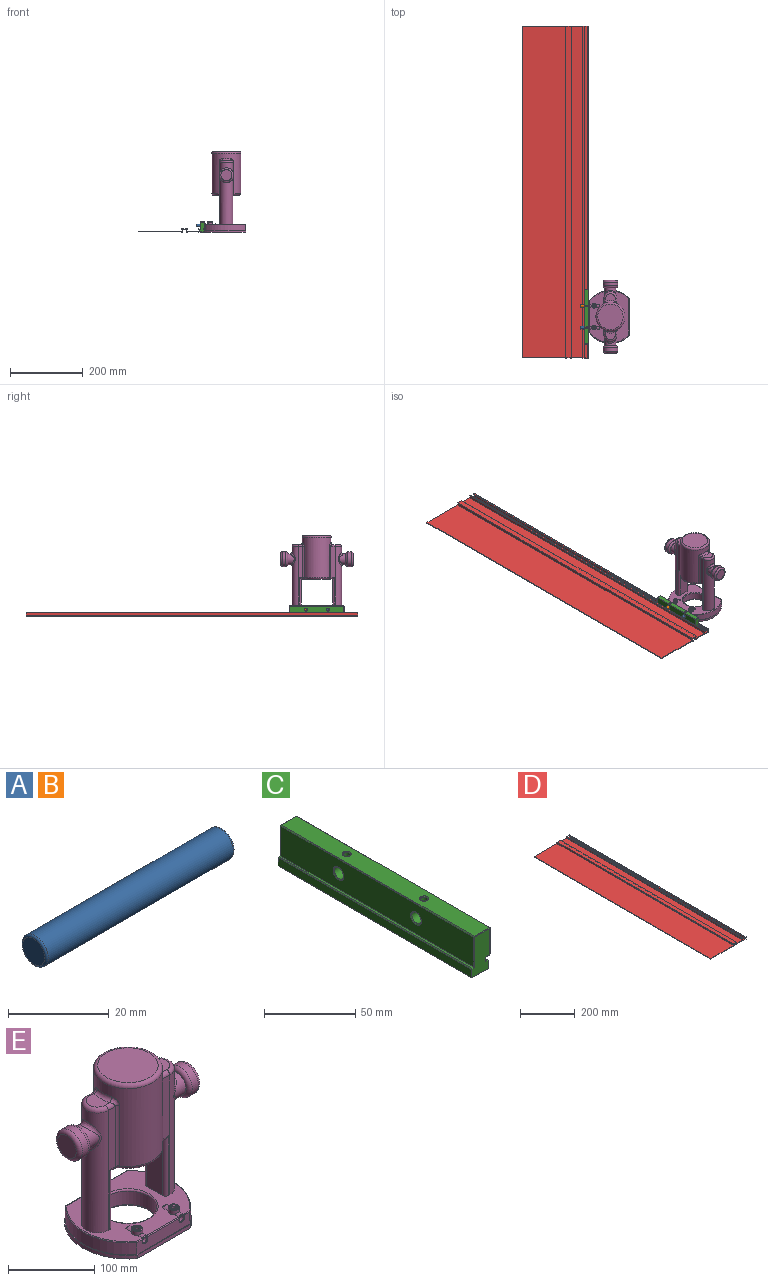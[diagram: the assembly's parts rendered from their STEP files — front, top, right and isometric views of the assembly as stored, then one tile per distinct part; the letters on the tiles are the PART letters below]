
ASSEMBLY  parts=5 mates=7
PART A: 5 faces, bbox 53x7.8x7.8 mm
  f0: cylinder r=3.6mm len=52mm, axis (-1,0,0), area 1174.6mm2, adj f3,f4
  f1: plane 6.19x6.19mm, normal (1,0,0), area 30.1mm2, adj f4
  f2: plane 6.19x6.19mm, normal (-1,0,0), area 30.1mm2, adj f3
  f3: torus R=3.1mm, axis (1,0,0), area 16.8mm2, adj f0,f2
  f4: torus R=3.1mm, axis (1,0,0), area 16.8mm2, adj f0,f1
PART B: same geometry as A
PART C: 48 faces, bbox 14.5x150x27 mm
  f0: plane 149x11.75mm, normal (0,0,1), area 1710.7mm2, adj f25,f28,f29,f30,f42,f43
  f1: cylinder r=3.65mm len=11.75mm, axis (1,0,0), area 256.1mm2, adj f14,f44,f47
  f2: plane 149x17.49mm, normal (1,0,0), area 2497.8mm2, adj f30,f33,f34,f35,f46,f47
  f3: plane 149x20mm, normal (-1,0,0), area 2871.9mm2, adj f4,f23,f24,f25,f44,f45
  f4: plane 149x1.25mm, normal (0,0,1), area 186.3mm2, adj f3,f20,f21,f22
  f5: plane 150x5.5mm, normal (-1,0,0), area 824.7mm2, adj f10,f11,f20,f39
  f6: plane 149x11.5mm, normal (0,0,-1), area 1713.2mm2, adj f38,f39,f40,f41
  f7: plane 150x5.5mm, normal (1,0,0), area 824.7mm2, adj f10,f11,f18,f40
  f8: plane 149x1.25mm, normal (0,0,1), area 186.2mm2, adj f9,f17,f18,f19
  f9: plane 149.5x3.01mm, normal (1,0,0), area 300.9mm2, adj f8,f11,f12,f16,f19,f37
  f10: plane 26x14mm, normal (0,1,0), area 300.2mm2, adj f5,f7,f12,f16,f17,f21,f23,f28
  f11: plane 26x14mm, normal (0,-1,0), area 299.8mm2, adj f5,f7,f9,f19,f22,f24,f29,f34
  f12: plane 149.5x3.75mm, normal (0,0,-1), area 486.1mm2, adj f9,f10,f16,f35,f37
  f13: cylinder r=3.65mm len=11.75mm, axis (1,0,0), area 256.1mm2, adj f15,f45,f46
  f14: cylinder r=2.02mm len=6.46mm, axis (0,0,1), area 78mm2, adj f1,f43
  f15: cylinder r=2.02mm len=6.46mm, axis (0,0,1), area 78mm2, adj f13,f42
  f16: plane 2.51x0.5mm, normal (0.71,0.71,0), area 1.6mm2, adj f9,f10,f12,f17
  f17: plane 2.25x0.5mm, normal (0,0.71,0.71), area 1.2mm2, adj f8,f10,f16,f18
  f18: plane 150x0.5mm, normal (0.71,0,0.71), area 105.7mm2, adj f7,f8,f17,f19
  f19: plane 1.75x0.5mm, normal (0,-0.71,0.71), area 1.1mm2, adj f8,f9,f11,f18
  f20: plane 150x0.5mm, normal (-0.71,0,0.71), area 105.7mm2, adj f4,f5,f21,f22
  f21: plane 2.25x0.5mm, normal (0,0.71,0.71), area 1.2mm2, adj f4,f10,f20,f23
  f22: plane 2.25x0.5mm, normal (0,-0.71,0.71), area 1.2mm2, adj f4,f11,f20,f24
  f23: plane 20.5x0.5mm, normal (-0.71,0.71,0), area 14.3mm2, adj f3,f10,f21,f26
  f24: plane 20.5x0.5mm, normal (-0.71,-0.71,0), area 14.3mm2, adj f3,f11,f22,f27
  f25: plane 149x0.5mm, normal (-0.71,0,0.71), area 105.4mm2, adj f0,f3,f26,f27
  f26: plane 0.5x0.5mm, normal (-0.58,0.58,0.58), area 0.2mm2, adj f23,f25,f28
  f27: plane 0.5x0.5mm, normal (-0.58,-0.58,0.58), area 0.2mm2, adj f24,f25,f29
  f28: plane 11.75x0.5mm, normal (0,0.71,0.71), area 8.3mm2, adj f0,f10,f26,f31
  f29: plane 11.75x0.5mm, normal (0,-0.71,0.71), area 8.3mm2, adj f0,f11,f27,f32
  f30: plane 149x0.5mm, normal (0.71,0,0.71), area 105.4mm2, adj f0,f2,f31,f32
  f31: plane 0.5x0.5mm, normal (0.58,0.58,0.58), area 0.2mm2, adj f28,f30,f33
  f32: plane 0.5x0.5mm, normal (0.58,-0.58,0.58), area 0.2mm2, adj f29,f30,f34
  f33: plane 17.99x0.5mm, normal (0.71,0.71,0), area 12.5mm2, adj f2,f10,f31,f35
  f34: plane 17.49x0.5mm, normal (0.71,-0.71,0), area 12.4mm2, adj f2,f11,f32,f36
  f35: plane 149.5x0.5mm, normal (0.71,0,-0.71), area 105.5mm2, adj f2,f12,f33,f36
  f36: plane 0.5x0.5mm, normal (0.58,-0.58,-0.58), area 0.2mm2, adj f34,f35,f37
  f37: plane 3.25x0.5mm, normal (0,-0.71,-0.71), area 2.3mm2, adj f9,f11,f12,f36
  f38: plane 12.5x0.5mm, normal (0,-0.71,-0.71), area 8.5mm2, adj f6,f11,f39,f40
  f39: plane 150x0.5mm, normal (-0.71,0,-0.71), area 105.7mm2, adj f5,f6,f38,f41
  f40: plane 150x0.5mm, normal (0.71,0,-0.71), area 105.7mm2, adj f6,f7,f38,f41
  f41: plane 12.5x0.5mm, normal (0,0.71,-0.71), area 8.5mm2, adj f6,f10,f39,f40
  f42: torus R=2.52mm, axis (0,0,-1), area 10.9mm2, adj f0,f15
  f43: torus R=2.52mm, axis (0,0,-1), area 10.9mm2, adj f0,f14
  f44: torus R=4.15mm, axis (1,0,0), area 18.9mm2, adj f1,f3
  f45: torus R=4.15mm, axis (1,0,0), area 18.9mm2, adj f3,f13
  f46: torus R=4.15mm, axis (1,0,0), area 18.9mm2, adj f2,f13
  f47: torus R=4.15mm, axis (1,0,0), area 18.9mm2, adj f1,f2
PART D: 34 faces, bbox 183.5x914.4x10.5 mm
  f0: plane 914.4x3.75mm, normal (0,0,1), area 3429mm2, adj f1,f31,f32,f33
  f1: plane 914.4x6.5mm, normal (-1,0,0), area 5943.6mm2, adj f0,f2,f32,f33
  f2: plane 914.4x32mm, normal (0,0,1), area 29260.8mm2, adj f1,f3,f32,f33
  f3: plane 914.4x6.5mm, normal (1,0,0), area 5943.6mm2, adj f2,f4,f32,f33
  f4: plane 914.4x16mm, normal (0,0,1), area 14630.4mm2, adj f3,f5,f32,f33
  f5: plane 914.4x6.5mm, normal (-1,0,0), area 5943.6mm2, adj f4,f6,f32,f33
  f6: plane 914.4x119mm, normal (0,0,1), area 108813.6mm2, adj f5,f7,f32,f33
  f7: plane 914.4x2mm, normal (-1,0,0), area 1828.8mm2, adj f6,f8,f32,f33
  f8: plane 914.4x119mm, normal (0,0,-1), area 108813.6mm2, adj f7,f9,f32,f33
  f9: plane 914.4x2mm, normal (-1,0,0), area 1828.8mm2, adj f8,f10,f32,f33
  f10: plane 914.4x3.75mm, normal (0,0,-1), area 3429mm2, adj f9,f11,f32,f33
  f11: plane 914.4x2mm, normal (1,0,0), area 1828.8mm2, adj f10,f12,f32,f33
  f12: plane 914.4x1.75mm, normal (0,0,1), area 1600.2mm2, adj f11,f13,f32,f33
  f13: plane 914.4x6.5mm, normal (1,0,0), area 5943.6mm2, adj f12,f14,f32,f33
  f14: plane 914.4x12mm, normal (0,0,-1), area 10972.8mm2, adj f13,f15,f32,f33
  f15: plane 914.4x6.5mm, normal (-1,0,0), area 5943.6mm2, adj f14,f16,f32,f33
  f16: plane 914.4x1.75mm, normal (0,0,1), area 1600.2mm2, adj f15,f17,f32,f33
  f17: plane 914.4x2mm, normal (-1,0,0), area 1828.8mm2, adj f16,f18,f32,f33
  f18: plane 914.4x3.75mm, normal (0,0,-1), area 3429mm2, adj f17,f19,f32,f33
  f19: plane 914.4x2mm, normal (1,0,0), area 1828.8mm2, adj f18,f20,f32,f33
  f20: plane 914.4x32mm, normal (0,0,-1), area 29260.8mm2, adj f19,f21,f32,f33
  f21: plane 914.4x2mm, normal (-1,0,0), area 1828.8mm2, adj f20,f22,f32,f33
  f22: plane 914.4x16.5mm, normal (0,0,-1), area 15087.6mm2, adj f21,f23,f32,f33
  f23: plane 914.4x10.5mm, normal (1,0,0), area 9601.2mm2, adj f22,f24,f32,f33
  f24: plane 914.4x3.75mm, normal (0,0,1), area 3429mm2, adj f23,f25,f32,f33
  f25: plane 914.4x2mm, normal (-1,0,0), area 1828.8mm2, adj f24,f26,f32,f33
  f26: plane 914.4x1.75mm, normal (0,0,-1), area 1600.2mm2, adj f25,f27,f32,f33
  f27: plane 914.4x6.5mm, normal (-1,0,0), area 5943.6mm2, adj f26,f28,f32,f33
  f28: plane 914.4x12.5mm, normal (0,0,1), area 11430mm2, adj f27,f29,f32,f33
  f29: plane 914.4x6.5mm, normal (1,0,0), area 5943.6mm2, adj f28,f30,f32,f33
  f30: plane 914.4x1.75mm, normal (0,0,-1), area 1600.2mm2, adj f29,f31,f32,f33
  f31: plane 914.4x2mm, normal (1,0,0), area 1828.8mm2, adj f0,f30,f32,f33
  f32: plane 183.5x10.5mm, normal (0,-1,0), area 449mm2, adj f0,f1,f2,f3,f4,f5,f6,f7
  f33: plane 183.5x10.5mm, normal (0,1,0), area 449mm2, adj f0,f1,f2,f3,f4,f5,f6,f7
PART E: 108 faces, bbox 200.6x119.7x223.6 mm
  f0: cylinder r=3.6mm len=28mm, axis (0,-1,0), area 607.3mm2, adj f89,f90,f97
  f1: plane 86.74x17mm, normal (0,-1,0), area 1357.1mm2, adj f15,f21,f23,f95,f97,f100,f102,f103
  f2: plane 143.61x108.61mm, normal (0,0,1), area 7962.3mm2, adj f3,f4,f5,f7,f8,f9,f10,f27
  f3: cylinder r=6.25mm len=12.5mm, axis (0,0,-1), area 209.6mm2, adj f2,f84,f86,f106
  f4: cylinder r=18mm len=170mm, axis (0,0,-1), area 8490.4mm2, adj f2,f7,f8,f42,f69
  f5: cylinder r=18mm len=170mm, axis (0,0,-1), area 8490.4mm2, adj f2,f9,f10,f33,f75
  f6: cylinder r=40mm len=110.52mm, axis (0,0,-1), area 19663.1mm2, adj f32,f34,f36,f37,f38,f39,f41,f43
  f7: plane 170x11.66mm, normal (0,-1,0), area 1163.2mm2, adj f2,f4,f44,f46,f47,f56
  f8: plane 170x11.66mm, normal (0,1,0), area 1163.2mm2, adj f2,f4,f39,f40,f48,f57
  f9: plane 170x11.66mm, normal (0,1,0), area 1163.2mm2, adj f2,f5,f31,f32,f49,f61
  f10: plane 170x11.66mm, normal (0,-1,0), area 1163.2mm2, adj f2,f5,f35,f38,f50,f52
  f11: plane 87.07x5mm, normal (0,-1,0), area 435.4mm2, adj f15,f16,f17,f20
  f12: cylinder r=73.5mm len=111.76mm, axis (0,0,-1), area 636.7mm2, adj f15,f16,f17,f18
  f13: plane 101.65x5mm, normal (0,1,0), area 508.2mm2, adj f15,f16,f18,f19
  f14: cylinder r=73.5mm len=111.76mm, axis (0,0,-1), area 636.7mm2, adj f15,f16,f19,f20
  f15: plane 147x112mm, normal (0,0,1), area 441.6mm2, adj f1,f11,f12,f13,f14,f17,f18,f19
  f16: plane 147x112mm, normal (0,0,-1), area 10820.1mm2, adj f11,f12,f13,f14,f17,f18,f19,f20
  f17: cylinder r=0.5mm len=5mm, axis (0,0,-1), area 1.6mm2, adj f11,f12,f15,f16
  f18: cylinder r=0.5mm len=5mm, axis (0,0,-1), area 1.9mm2, adj f12,f13,f15,f16
  f19: cylinder r=0.5mm len=5mm, axis (0,0,-1), area 1.9mm2, adj f13,f14,f15,f16
  f20: cylinder r=0.5mm len=5mm, axis (0,0,-1), area 1.6mm2, adj f11,f14,f15,f16
  f21: cylinder r=72.5mm len=110mm, axis (0,0,-1), area 2129.1mm2, adj f1,f15,f22,f99
  f22: plane 101.24x17mm, normal (0,1,0), area 1721.1mm2, adj f15,f21,f23,f96
  f23: cylinder r=72.5mm len=110mm, axis (0,0,-1), area 2129.1mm2, adj f1,f15,f22,f94
  f24: plane 70x70mm, normal (0,0,1), area 3848.5mm2, adj f51
  f25: plane 26x20.26mm, normal (0,0,1), area 420.7mm2, adj f40,f42,f43,f44
  f26: plane 26x20.26mm, normal (0,0,1), area 420.7mm2, adj f31,f33,f35,f36
  f27: plane 79.48x26mm, normal (-1,0,0), area 2066.6mm2, adj f2,f28,f47,f48
  f28: plane 86.74x70mm, normal (0,0,-1), area 4350.4mm2, adj f27,f29,f52,f53,f54,f55,f56,f57
  f29: plane 79.48x26mm, normal (1,0,0), area 2066.6mm2, adj f2,f28,f49,f50
  f30: cylinder r=33mm len=66mm, axis (0,0,-1), area 3939.6mm2, adj f76,f77
  f31: cylinder r=5mm len=11.66mm, axis (1,0,0), area 77.4mm2, adj f9,f26,f33,f34
  f32: cylinder r=5mm len=85.52mm, axis (0,0,-1), area 442.3mm2, adj f6,f9,f34,f60
  f33: torus R=13mm, axis (0,0,1), area 399.3mm2, adj f5,f26,f31,f35
  f34: bspline ~11.98x9.88mm, area 72.2mm2, adj f6,f31,f32,f36
  f35: cylinder r=5mm len=11.66mm, axis (-1,0,0), area 77.4mm2, adj f10,f26,f33,f37
  f36: torus R=45mm, axis (0,0,1), area 192.5mm2, adj f6,f26,f34,f37
  f37: bspline ~10.88x10.63mm, area 72.2mm2, adj f6,f35,f36,f38
  f38: cylinder r=5mm len=85.52mm, axis (0,0,-1), area 442.3mm2, adj f6,f10,f37,f53
  f39: cylinder r=5mm len=85.52mm, axis (0,0,-1), area 442.3mm2, adj f6,f8,f41,f58
  f40: cylinder r=5mm len=11.66mm, axis (1,0,0), area 77.4mm2, adj f8,f25,f41,f42
  f41: bspline ~10.88x10.63mm, area 72.2mm2, adj f6,f39,f40,f43
  f42: torus R=13mm, axis (0,0,1), area 399.3mm2, adj f4,f25,f40,f44
  f43: torus R=45mm, axis (0,0,1), area 192.5mm2, adj f6,f25,f41,f45
  f44: cylinder r=5mm len=11.66mm, axis (-1,0,0), area 77.4mm2, adj f7,f25,f42,f45
  f45: bspline ~11.98x9.88mm, area 72.2mm2, adj f6,f43,f44,f46
  f46: cylinder r=5mm len=85.52mm, axis (0,0,-1), area 442.3mm2, adj f6,f7,f45,f55
  f47: cylinder r=5mm len=84.48mm, axis (0,0,-1), area 638.5mm2, adj f2,f7,f27,f56
  f48: cylinder r=5mm len=84.48mm, axis (0,0,1), area 638.5mm2, adj f2,f8,f27,f57
  f49: cylinder r=5mm len=84.48mm, axis (0,0,-1), area 638.5mm2, adj f2,f9,f29,f61
  f50: cylinder r=5mm len=84.48mm, axis (0,0,1), area 638.5mm2, adj f2,f10,f29,f52
  f51: torus R=35mm, axis (0,0,1), area 1884.3mm2, adj f6,f24
  f52: cylinder r=5mm len=9.69mm, axis (1,0,0), area 51.1mm2, adj f10,f28,f50,f53
  f53: torus R=10mm, axis (0,0,-1), area 55.4mm2, adj f28,f38,f52,f54
  f54: torus R=35mm, axis (0,0,-1), area 620.4mm2, adj f6,f28,f53,f55
  f55: torus R=10mm, axis (0,0,-1), area 55.4mm2, adj f28,f46,f54,f56
  f56: cylinder r=5mm len=9.69mm, axis (1,0,0), area 51.1mm2, adj f7,f28,f47,f55
  f57: cylinder r=5mm len=9.69mm, axis (-1,0,0), area 51.1mm2, adj f8,f28,f48,f58
  f58: torus R=10mm, axis (0,0,-1), area 55.4mm2, adj f28,f39,f57,f59
  f59: torus R=35mm, axis (0,0,-1), area 620.4mm2, adj f6,f28,f58,f60
  f60: torus R=10mm, axis (0,0,-1), area 55.4mm2, adj f28,f32,f59,f61
  f61: cylinder r=5mm len=9.69mm, axis (-1,0,0), area 51.1mm2, adj f9,f28,f49,f60
  f62: cylinder r=15mm len=30mm, axis (-1,0,0), area 1129.4mm2, adj f72,f75
  f63: cylinder r=15mm len=30mm, axis (-1,0,0), area 1129.8mm2, adj f66,f69
  f64: cylinder r=20.31mm len=40.63mm, axis (-1,0,0), area 1276.4mm2, adj f67,f68
  f65: plane 30.63x30.63mm, normal (1,0,0), area 736.8mm2, adj f68
  f66: plane 30.63x30.63mm, normal (-1,0,0), area 29.9mm2, adj f63,f67
  f67: torus R=15.31mm, axis (1,0,0), area 912.8mm2, adj f64,f66
  f68: torus R=15.31mm, axis (1,0,0), area 912.8mm2, adj f64,f65
  f69: bspline ~40.02x31.31mm, area 576.1mm2, adj f4,f63
  f70: cylinder r=20.31mm len=40.63mm, axis (1,0,0), area 1276.4mm2, adj f73,f74
  f71: plane 30.63x30.63mm, normal (-1,0,0), area 736.8mm2, adj f74
  f72: plane 30.63x30.63mm, normal (1,0,0), area 29.9mm2, adj f62,f73
  f73: torus R=15.31mm, axis (-1,0,0), area 912.8mm2, adj f70,f72
  f74: torus R=15.31mm, axis (-1,0,0), area 912.8mm2, adj f70,f71
  f75: bspline ~40.02x31.31mm, area 576.1mm2, adj f5,f62
  f76: torus R=35mm, axis (0,0,1), area 665.7mm2, adj f2,f30
  f77: torus R=35mm, axis (0,0,1), area 665.7mm2, adj f16,f30
  f78: cylinder r=6.25mm len=12.5mm, axis (0,0,-1), area 209.6mm2, adj f2,f81,f83,f107
  f79: plane 10.5x10.5mm, normal (0,0,1), area 42.4mm2, adj f92,f107
  f80: plane 10.5x10.5mm, normal (0,0,1), area 42.4mm2, adj f93,f106
  f81: cylinder r=5.5mm len=9.46mm, axis (0,-1,0), area 71.8mm2, adj f2,f78,f105
  f82: plane 4.12x0.5mm, normal (0,1,0), area 1.4mm2, adj f2,f105
  f83: cylinder r=5.5mm len=7.55mm, axis (0,-1,0), area 52mm2, adj f2,f78,f98
  f84: cylinder r=5.5mm len=9.46mm, axis (0,-1,0), area 71.8mm2, adj f2,f3,f104
  f85: plane 4.12x0.5mm, normal (0,1,0), area 1.4mm2, adj f2,f104
  f86: cylinder r=5.5mm len=7.55mm, axis (0,-1,0), area 52mm2, adj f2,f3,f101
  f87: cylinder r=3.6mm len=28mm, axis (0,-1,0), area 607.3mm2, adj f88,f91,f103
  f88: plane 7.2x7.2mm, normal (0,-1,0), area 40.7mm2, adj f87
  f89: plane 7.2x7.2mm, normal (0,-1,0), area 40.7mm2, adj f0
  f90: cylinder r=2.75mm len=7.43mm, axis (0,0,1), area 116.7mm2, adj f0,f92
  f91: cylinder r=2.75mm len=7.43mm, axis (0,0,1), area 116.7mm2, adj f87,f93
  f92: torus R=3.75mm, axis (0,0,1), area 30.7mm2, adj f79,f90
  f93: torus R=3.75mm, axis (0,0,1), area 30.7mm2, adj f80,f91
  f94: torus R=71.5mm, axis (0,0,1), area 195.2mm2, adj f2,f23,f95,f96
  f95: cylinder r=1mm len=9.99mm, axis (-1,0,0), area 15.1mm2, adj f1,f2,f94,f97,f98
  f96: cylinder r=1mm len=101.24mm, axis (1,0,0), area 158.4mm2, adj f2,f22,f94,f99
  f97: torus R=4.6mm, axis (0,1,0), area 38.7mm2, adj f0,f1,f95,f98,f100
  f98: torus R=4.5mm, axis (0,1,0), area 12.5mm2, adj f83,f95,f97,f100
  f99: torus R=71.5mm, axis (0,0,1), area 195.2mm2, adj f2,f21,f96,f102
  f100: cylinder r=1mm len=53.25mm, axis (-1,0,0), area 82.9mm2, adj f1,f2,f97,f98,f101,f103
  f101: torus R=4.5mm, axis (0,1,0), area 12.5mm2, adj f86,f100,f102,f103
  f102: cylinder r=1mm len=9.99mm, axis (-1,0,0), area 15.1mm2, adj f1,f2,f99,f101,f103
  f103: torus R=4.6mm, axis (0,1,0), area 38.7mm2, adj f1,f87,f100,f101,f102
  f104: torus R=4.5mm, axis (0,-1,0), area 10mm2, adj f2,f84,f85
  f105: torus R=4.5mm, axis (0,-1,0), area 10mm2, adj f2,f81,f82
  f106: torus R=5.25mm, axis (0,0,1), area 58.1mm2, adj f3,f80
  f107: torus R=5.25mm, axis (0,0,1), area 58.1mm2, adj f78,f79
PLACE A rot(axis=(0,0,-1),180deg) t=(214,83.38,17)mm
PLACE B rot(axis=(-1,0,0),180deg) t=(160.5,143.38,17)mm
PLACE C t=(183.5,952.78,0)mm
PLACE D t=(183.5,914.4,0)mm
PLACE E rot(axis=(0,0,-1),90deg) t=(242.6,113.38,-2)mm
MATE planar D.f23 <-> E.f11  axis (1,0,0) through (183.5,457.2,3.25)mm
MATE cylindrical C.f1 <-> A.f0  axis (1,0,0) through (183,83.38,17)mm
MATE planar D.f29 <-> C.f5  axis (1,0,0) through (169,0,3.25)mm
MATE cylindrical C.f45 <-> B.f0  axis (1,0,0) through (183,143.38,17)mm
MATE fastened E.f0 <-> B.f0  axis (-1,0,0) through (213.5,143.38,17)mm
MATE fastened E.f101 <-> A.f0  axis (-1,0,0) through (213.5,83.38,17)mm
MATE planar D.f28 <-> C.f6  axis (0,0,1) through (175.25,0,0)mm
